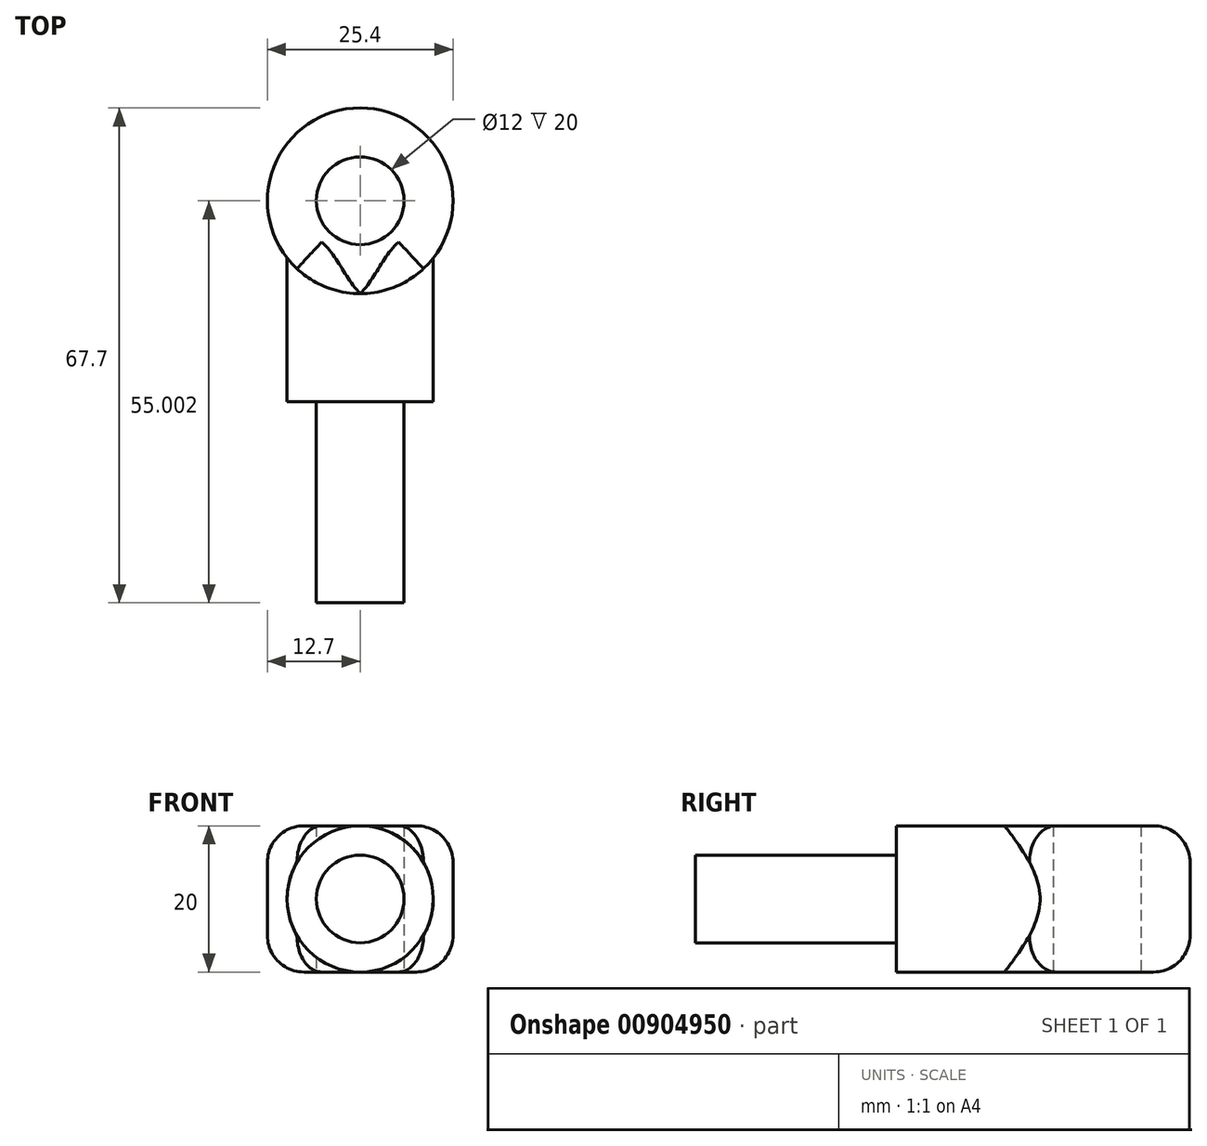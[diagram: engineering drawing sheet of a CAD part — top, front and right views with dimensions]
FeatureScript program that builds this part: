
annotation { "Feature Type Name" : "Feature", "Feature Type Description" : "" }
export const myFeature = defineFeature(function(context is Context, id is Id, definition is map)
    precondition{}
    {
        {
            var Q0;
            Q0=qCreatedBy(makeId("Top.planeOp"),FACE);
            var sketch = newSketch(context, id + "F0", { "sketchPlane" : qUnion([Q0])});
            skLineSegment(sketch, "E0", {"start": v(0, -44.18) * mm, "end": v(0, 10.82) * mm});
            skCircle(sketch, "E1", {"center": v(0, 10.82) * mm, "radius": 6 * mm});
            skCircle(sketch, "E2", {"center": v(0, 10.82) * mm, "radius": 12.7 * mm});
            skLineSegment(sketch, "E3", {"start": v(0, -44.18) * mm, "end": v(6, -44.18) * mm});
            skLineSegment(sketch, "E4", {"start": v(0, -16.68) * mm, "end": v(10, -16.68) * mm});
            skSolve(sketch);
        }
        {
            var Q0;
            Q0=sQuery(id+"F0.wireOp",EDGE,"E3");
            var Q1;
            Q1=sQuery(id+"F0.wireOp",EDGE,"E0");
            revolve(context, id + "F1", {"bodyType" : ToolBodyType.SURFACE, "surfaceOperationType" : NewSurfaceOperationType.NEW, "surfaceEntities" : qUnion([Q0]), "axis" : qUnion([Q1]), "revolveType" : RevolveType.FULL});
        }
        {
            var Q0;
            Q0=sQuery(id+"F0.wireOp",EDGE,"E4");
            var Q1;
            Q1=sQuery(id+"F0.wireOp",EDGE,"E0");
            revolve(context, id + "F2", {"bodyType" : ToolBodyType.SURFACE, "surfaceOperationType" : NewSurfaceOperationType.NEW, "surfaceEntities" : qUnion([Q0]), "axis" : qUnion([Q1]), "revolveType" : RevolveType.FULL});
        }
        {
            var Q0;
            Q0=makeQuery(id+"F1.opRevolve","SWEPT_FACE",FACE,{"disambiguationData":[OSD([sQuery(id+"F0.wireOp",EDGE,"E3")])]});
            extrude(context, id + "F3", {"entities" : qUnion([Q0]), "depth" : 27.6 * mm, "offsetDistance" : 25 * mm});
        }
        {
            var Q0;
            Q0=makeQuery(id+"F2.opRevolve","SWEPT_FACE",FACE,{"disambiguationData":[OSD([sQuery(id+"F0.wireOp",EDGE,"E4")])]});
            extrude(context, id + "F4", {"entities" : qUnion([Q0]), "operationType" : NewBodyOperationType.ADD, "depth" : 20.6 * mm, "offsetDistance" : 25 * mm});
        }
        {
            var Q0;
            Q0=makeQuery(id+"F0.imprint","IMPRINT",FACE,{"disambiguationData":[TD([[makeQuery(id+"F0.imprint","IMPRINT",EDGE,{"derivedFrom":sQuery(id+"F0.wireOp",EDGE,"E1")}),-1.0]])]});
            extrude(context, id + "F5", {"entities" : qUnion([Q0]), "operationType" : NewBodyOperationType.ADD, "endBound" : BoundingType.SYMMETRIC, "depth" : 20 * mm, "offsetDistance" : 25 * mm});
        }
        {
            var Q0;
            Q0=makeQuery(id+"F5.opExtrude","CAP_EDGE",EDGE,{"disambiguationData":[OSD([sQuery(id+"F0.wireOp",EDGE,"E2")])],"isStart":true});
            fillet(context, id + "F6", {"entities" : qUnion([Q0]), "radius" : 5 * mm, "tangentPropagation" : true, "allowEdgeOverflow" : false});
        }
        {
            var Q0;
            Q0=makeQuery(id+"F5.opExtrude","CAP_EDGE",EDGE,{"disambiguationData":[OSD([sQuery(id+"F0.wireOp",EDGE,"E2")])],"isStart":false});
            fillet(context, id + "F7", {"entities" : qUnion([Q0]), "radius" : 5 * mm, "tangentPropagation" : true, "allowEdgeOverflow" : false});
        }
    });
